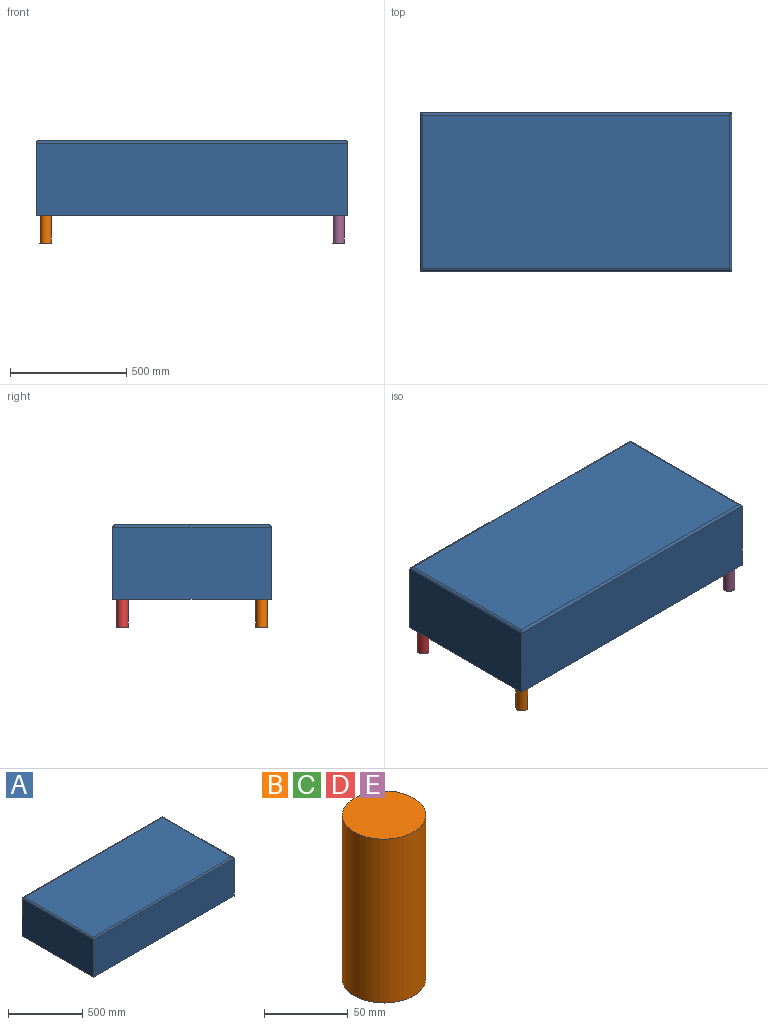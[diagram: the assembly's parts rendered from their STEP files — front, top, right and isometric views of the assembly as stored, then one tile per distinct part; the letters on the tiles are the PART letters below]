
ASSEMBLY  parts=5 mates=4
PART A: 10 faces, bbox 1340x680x320 mm
  f0: plane 680x310mm, normal (-1,0,0), area 210800mm2, adj f1,f3,f5,f6
  f1: plane 1340x310mm, normal (0,-1,0), area 415400mm2, adj f0,f2,f5,f8
  f2: plane 680x310mm, normal (1,0,0), area 210800mm2, adj f1,f3,f5,f9
  f3: plane 1340x310mm, normal (0,1,0), area 415400mm2, adj f0,f2,f5,f7
  f4: plane 1320x660mm, normal (0,0,1), area 871200mm2, adj f6,f7,f8,f9
  f5: plane 1340x680mm, normal (0,0,-1), area 911200mm2, adj f0,f1,f2,f3
  f6: cylinder r=10mm len=680mm, axis (0,1,0), area 10567.3mm2, adj f0,f4,f7,f8
  f7: cylinder r=10mm len=1340mm, axis (1,0,0), area 20934.5mm2, adj f3,f4,f6,f9
  f8: cylinder r=10mm len=1340mm, axis (-1,0,0), area 20934.5mm2, adj f1,f4,f6,f9
  f9: cylinder r=10mm len=680mm, axis (0,-1,0), area 10567.3mm2, adj f2,f4,f7,f8
PART B: 3 faces, bbox 50x50x120 mm
  f0: cylinder r=25mm len=120mm, axis (0,0,-1), area 18849.6mm2, adj f1,f2
  f1: plane 50x50mm, normal (0,0,1), area 1963.5mm2, adj f0
  f2: plane 50x50mm, normal (0,0,-1), area 1963.5mm2, adj f0
PART C: same geometry as B
PART D: same geometry as B
PART E: same geometry as B
PLACE A t=(-80.62,6.25,15.74)mm
PLACE B t=(-703.65,-225.36,-104.26)mm
PLACE C t=(556.35,374.64,-104.26)mm
PLACE D t=(-703.65,374.64,-104.26)mm
PLACE E t=(556.35,-225.36,-104.26)mm
MATE fastened D.f0 <-> A.f5  axis (0,0,1) through (-703.65,374.64,15.74)mm
MATE fastened C.f0 <-> A.f5  axis (0,0,1) through (556.35,374.64,15.74)mm
MATE fastened E.f0 <-> A.f5  axis (0,0,1) through (556.35,-225.36,15.74)mm
MATE fastened B.f0 <-> A.f5  axis (0,0,1) through (-703.65,-225.36,15.74)mm
